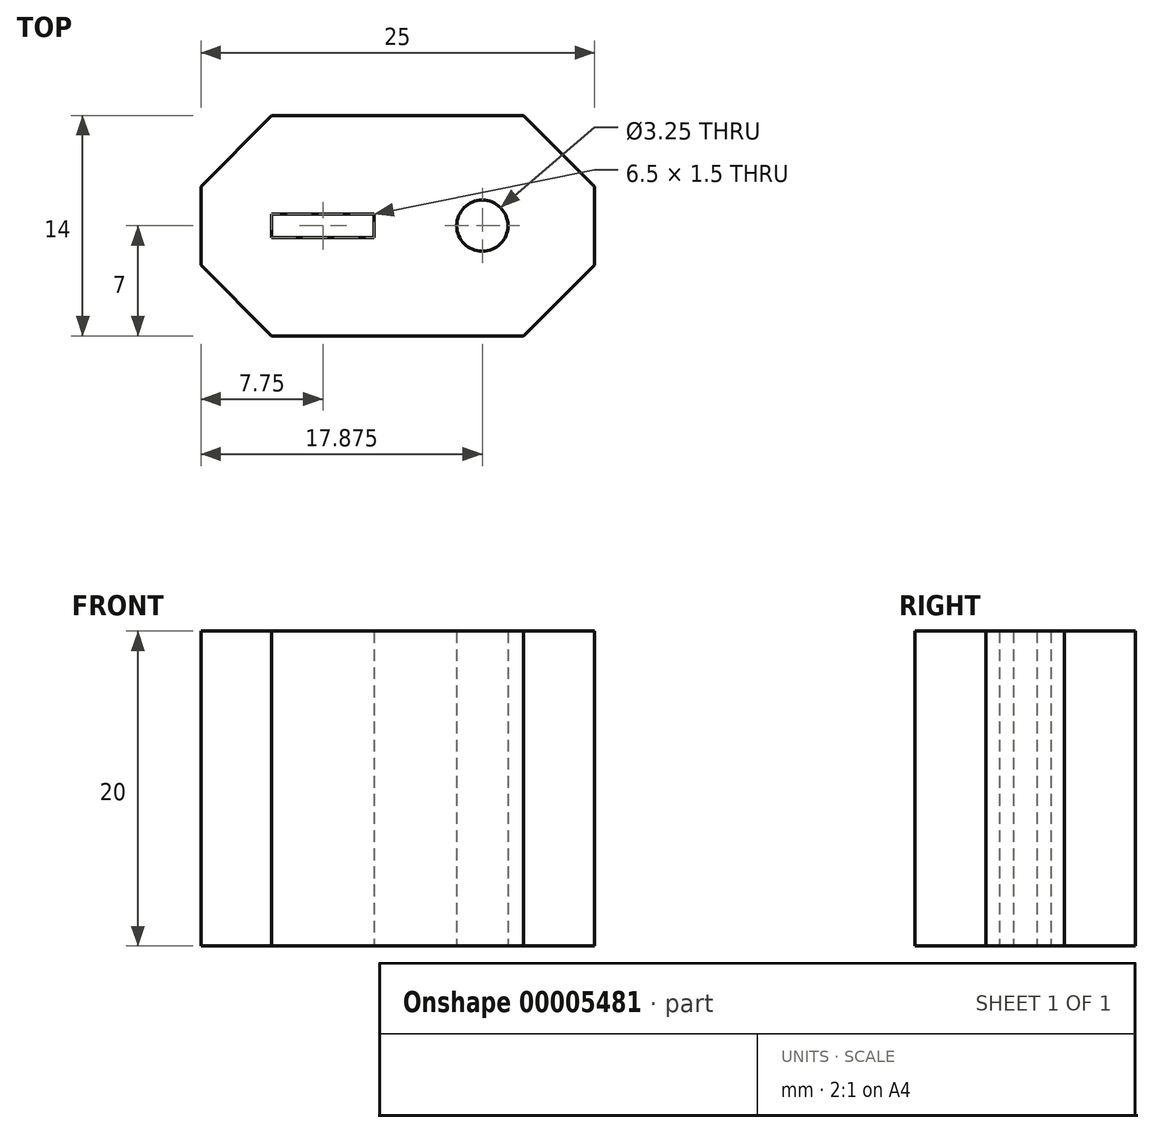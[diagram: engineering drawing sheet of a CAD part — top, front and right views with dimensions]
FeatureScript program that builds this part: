
annotation { "Feature Type Name" : "Feature", "Feature Type Description" : "" }
export const myFeature = defineFeature(function(context is Context, id is Id, definition is map)
    precondition{}
    {
        {
            var Q0;
            Q0=qCreatedBy(makeId("Top.planeOp"),FACE);
            var sketch = newSketch(context, id + "F0", { "sketchPlane" : qUnion([Q0])});
            skLineSegment(sketch, "E0.bottom", {"start": v(12.5, -7) * mm, "end": v(-12.5, -7) * mm});
            skLineSegment(sketch, "E0.top", {"start": v(12.5, 7) * mm, "end": v(-12.5, 7) * mm});
            skLineSegment(sketch, "E0.left", {"start": v(12.5, -7) * mm, "end": v(12.5, 7) * mm});
            skLineSegment(sketch, "E0.right", {"start": v(-12.5, -7) * mm, "end": v(-12.5, 7) * mm});
            skPoint(sketch, "E0.middle", {"position": v(0, 0) * mm});
            skLineSegment(sketch, "E1.bottom", {"start": v(-1.5, -0.75) * mm, "end": v(-8, -0.75) * mm});
            skLineSegment(sketch, "E1.top", {"start": v(-1.5, 0.75) * mm, "end": v(-8, 0.75) * mm});
            skLineSegment(sketch, "E1.left", {"start": v(-1.5, -0.75) * mm, "end": v(-1.5, 0.75) * mm});
            skLineSegment(sketch, "E1.right", {"start": v(-8, -0.75) * mm, "end": v(-8, 0.75) * mm});
            skPoint(sketch, "E1.middle", {"position": v(-4.75, 0) * mm});
            skCircle(sketch, "E2", {"center": v(5.38, 0) * mm, "radius": 1.63 * mm});
            skSolve(sketch);
        }
        {
            var Q0;
            Q0=makeQuery(id+"F0.imprint","IMPRINT",FACE,{"disambiguationData":[TD([[makeQuery(id+"F0.imprint","IMPRINT",EDGE,{"derivedFrom":sQuery(id+"F0.wireOp",EDGE,"E0.bottom")}),-1.0]])]});
            extrude(context, id + "F1", {"entities" : qUnion([Q0]), "depth" : 20 * mm});
        }
        {
            var Q0;
            Q0=makeQuery(id+"F1.opExtrude","SWEPT_EDGE",EDGE,{"disambiguationData":[OSD([sQuery(id+"F0.wireOp",EDGE,"E0.bottom"),sQuery(id+"F0.wireOp",EDGE,"E0.left")])]});
            var Q1;
            Q1=makeQuery(id+"F1.opExtrude","SWEPT_EDGE",EDGE,{"disambiguationData":[OSD([sQuery(id+"F0.wireOp",EDGE,"E0.top"),sQuery(id+"F0.wireOp",EDGE,"E0.left")])]});
            var Q2;
            Q2=makeQuery(id+"F1.opExtrude","SWEPT_EDGE",EDGE,{"disambiguationData":[OSD([sQuery(id+"F0.wireOp",EDGE,"E0.bottom"),sQuery(id+"F0.wireOp",EDGE,"E0.right")])]});
            var Q3;
            Q3=makeQuery(id+"F1.opExtrude","SWEPT_EDGE",EDGE,{"disambiguationData":[OSD([sQuery(id+"F0.wireOp",EDGE,"E0.top"),sQuery(id+"F0.wireOp",EDGE,"E0.right")])]});
            chamfer(context, id + "F2", {"entities" : qUnion([Q0, Q1, Q2, Q3]), "width" : 4.5 * mm, "tangentPropagation" : true});
        }
    });
